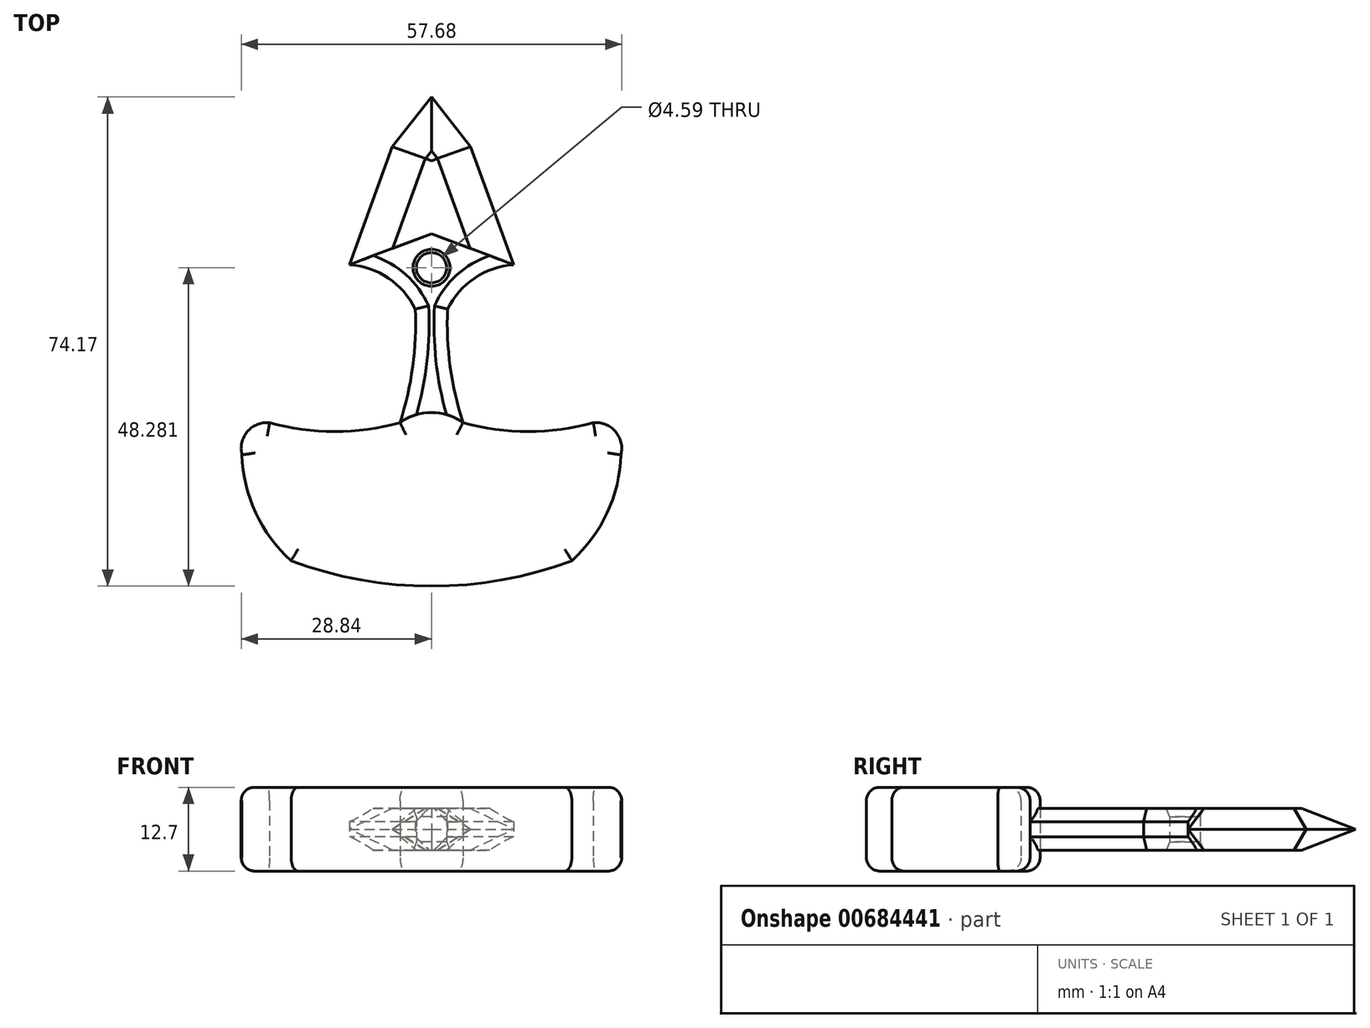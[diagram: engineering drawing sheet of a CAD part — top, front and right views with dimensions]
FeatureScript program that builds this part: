
annotation { "Feature Type Name" : "Feature", "Feature Type Description" : "" }
export const myFeature = defineFeature(function(context is Context, id is Id, definition is map)
    precondition{}
    {
        {
            var Q0;
            Q0=qCreatedBy(makeId("Top.planeOp"),FACE);
            var sketch = newSketch(context, id + "F0", { "sketchPlane" : qUnion([Q0])});
            skPoint(sketch, "E0.middle", {"position": v(0, 0) * mm});
            skLineSegment(sketch, "E1", {"start": v(0, 38.1) * mm, "end": v(5.93, 30.59) * mm});
            skLineSegment(sketch, "E2", {"start": v(5.93, 30.59) * mm, "end": v(12.44, 12.68) * mm});
            skLineSegment(sketch, "E3.MirrorCS", {"start": v(0, 38.1) * mm, "end": v(-5.93, 30.59) * mm});
            skLineSegment(sketch, "E4.MirrorCS", {"start": v(-5.93, 30.59) * mm, "end": v(-12.44, 12.68) * mm});
            skArc(sketch, "E5", {"start": v(-2.44, 5.93) * mm, "mid": v(-6.54, 10.65) * mm, "end": v(-12.44, 12.68) * mm});
            skArc(sketch, "E6.MirrorCS", {"start": v(2.44, 5.93) * mm, "mid": v(6.54, 10.65) * mm, "end": v(12.44, 12.68) * mm});
            skArc(sketch, "E7", {"start": v(2.44, 5.93) * mm, "mid": v(2.84, -2.78) * mm, "end": v(4.77, -11.28) * mm});
            skArc(sketch, "E8.MirrorCS", {"start": v(-2.44, 5.93) * mm, "mid": v(-2.84, -2.78) * mm, "end": v(-4.77, -11.28) * mm});
            skArc(sketch, "E9", {"start": v(4.77, -11.28) * mm, "mid": v(14.65, -12.62) * mm, "end": v(24.54, -11.28) * mm});
            skArc(sketch, "E10", {"start": v(28.72, -16.16) * mm, "mid": v(27.9, -12.64) * mm, "end": v(24.54, -11.28) * mm});
            skArc(sketch, "E11", {"start": v(21.28, -32.21) * mm, "mid": v(26.64, -24.95) * mm, "end": v(28.72, -16.16) * mm});
            skArc(sketch, "E12.MirrorCS", {"start": v(-4.77, -11.28) * mm, "mid": v(-14.65, -12.62) * mm, "end": v(-24.54, -11.28) * mm});
            skArc(sketch, "E13.MirrorCS", {"start": v(-28.72, -16.16) * mm, "mid": v(-27.9, -12.64) * mm, "end": v(-24.54, -11.28) * mm});
            skArc(sketch, "E14.MirrorCS", {"start": v(-21.28, -32.21) * mm, "mid": v(-26.64, -24.95) * mm, "end": v(-28.72, -16.16) * mm});
            skArc(sketch, "E15", {"start": v(-21.28, -32.21) * mm, "mid": v(0, -36.07) * mm, "end": v(21.28, -32.21) * mm});
            skArc(sketch, "E16", {"start": v(4.77, -11.28) * mm, "mid": v(0, -9.74) * mm, "end": v(-4.77, -11.28) * mm});
            skLineSegment(sketch, "E17", {"start": v(-5.93, 30.59) * mm, "end": v(0, 28.43) * mm});
            skLineSegment(sketch, "E18", {"start": v(0, 28.43) * mm, "end": v(5.93, 30.59) * mm});
            skLineSegment(sketch, "E19", {"start": v(-12.44, 12.68) * mm, "end": v(0, 17.33) * mm});
            skLineSegment(sketch, "E20", {"start": v(0, 17.33) * mm, "end": v(12.44, 12.68) * mm});
            skLineSegment(sketch, "E21", {"start": v(0, 38.1) * mm, "end": v(0, 28.43) * mm});
            skLineSegment(sketch, "E22", {"start": v(0, 17.33) * mm, "end": v(0, 28.43) * mm});
            skCircle(sketch, "E23", {"center": v(0, 12.21) * mm, "radius": 2.3 * mm});
            skSolve(sketch);
        }
        {
            var Q0;
            Q0=makeQuery(id+"F0.imprint","IMPRINT",FACE,{"disambiguationData":[TD([[makeQuery(id+"F0.imprint","IMPRINT",EDGE,{"derivedFrom":sQuery(id+"F0.wireOp",EDGE,"E9")}),-1.0]])]});
            extrude(context, id + "F1", {"entities" : qUnion([Q0]), "depth" : 12.7 * mm, "offsetDistance" : 25.4 * mm});
        }
        {
            var Q0;
            Q0=makeQuery(id+"F0.imprint","IMPRINT",FACE,{"disambiguationData":[TD([[makeQuery(id+"F0.imprint","IMPRINT",EDGE,{"derivedFrom":sQuery(id+"F0.wireOp",EDGE,"E5")}),-1.0]])]});
            extrude(context, id + "F2", {"entities" : qUnion([Q0]), "depth" : 6.35 * mm, "offsetDistance" : 25.4 * mm});
        }
        {
            var Q0;
            Q0=makeQuery(id+"F2.opExtrude","SWEPT_BODY",BODY,{"disambiguationData":[OSD([sQuery(id+"F0.wireOp",EDGE,"E5"),sQuery(id+"F0.wireOp",EDGE,"E6.MirrorCS"),sQuery(id+"F0.wireOp",EDGE,"E7"),sQuery(id+"F0.wireOp",EDGE,"E8.MirrorCS"),sQuery(id+"F0.wireOp",EDGE,"E16"),sQuery(id+"F0.wireOp",EDGE,"E19"),sQuery(id+"F0.wireOp",EDGE,"E20"),sQuery(id+"F0.wireOp",EDGE,"E23")])]});
            transform(context, id + "F3", {"entities" : qUnion([Q0]), "transformType" : TransformType.TRANSLATION_3D, "dx" : 0 * mm, "dy" : 0 * mm, "dz" : 3.17 * mm, "makeCopy" : false});
        }
        {
            var Q0;
            Q0=makeQuery(id+"F0.imprint","IMPRINT",FACE,{"disambiguationData":[TD([[makeQuery(id+"F0.imprint","IMPRINT",EDGE,{"derivedFrom":sQuery(id+"F0.wireOp",EDGE,"E2")}),-1.0]])]});
            var Q1;
            Q1=makeQuery(id+"F0.imprint","IMPRINT",FACE,{"disambiguationData":[TD([[makeQuery(id+"F0.imprint","IMPRINT",EDGE,{"derivedFrom":sQuery(id+"F0.wireOp",EDGE,"E4.MirrorCS")}),1.0]])]});
            extrude(context, id + "F4", {"entities" : qUnion([Q0, Q1]), "depth" : 6.35 * mm, "offsetDistance" : 25.4 * mm});
        }
        {
            var Q0;
            Q0=makeQuery(id+"F4.opExtrude","SWEPT_BODY",BODY,{"disambiguationData":[OSD([sQuery(id+"F0.wireOp",EDGE,"E2"),sQuery(id+"F0.wireOp",EDGE,"E4.MirrorCS"),sQuery(id+"F0.wireOp",EDGE,"E17"),sQuery(id+"F0.wireOp",EDGE,"E18"),sQuery(id+"F0.wireOp",EDGE,"E19"),sQuery(id+"F0.wireOp",EDGE,"E20")])]});
            transform(context, id + "F5", {"entities" : qUnion([Q0]), "transformType" : TransformType.TRANSLATION_3D, "dx" : 0 * mm, "dy" : 0 * mm, "dz" : 3.17 * mm, "makeCopy" : false});
        }
        {
            var Q0;
            Q0=makeQuery(id+"F0.imprint","IMPRINT",FACE,{"disambiguationData":[TD([[makeQuery(id+"F0.imprint","IMPRINT",EDGE,{"derivedFrom":sQuery(id+"F0.wireOp",EDGE,"E1")}),-1.0]])]});
            var Q1;
            Q1=makeQuery(id+"F0.imprint","IMPRINT",FACE,{"disambiguationData":[TD([[makeQuery(id+"F0.imprint","IMPRINT",EDGE,{"derivedFrom":sQuery(id+"F0.wireOp",EDGE,"E3.MirrorCS")}),1.0]])]});
            extrude(context, id + "F6", {"entities" : qUnion([Q0, Q1]), "depth" : 6.35 * mm, "offsetDistance" : 25.4 * mm});
        }
        {
            var Q0;
            Q0=makeQuery(id+"F6.opExtrude","SWEPT_BODY",BODY,{"disambiguationData":[OSD([sQuery(id+"F0.wireOp",EDGE,"E1"),sQuery(id+"F0.wireOp",EDGE,"E3.MirrorCS"),sQuery(id+"F0.wireOp",EDGE,"E17"),sQuery(id+"F0.wireOp",EDGE,"E18")])]});
            transform(context, id + "F7", {"entities" : qUnion([Q0]), "transformType" : TransformType.TRANSLATION_3D, "dx" : 0 * mm, "dy" : 0 * mm, "dz" : 3.17 * mm, "makeCopy" : false});
        }
        {
            var Q0;
            Q0=makeQuery(id+"F6.opExtrude","CAP_EDGE",EDGE,{"disambiguationData":[OSD([sQuery(id+"F0.wireOp",EDGE,"E1")])],"isStart":false});
            var Q1;
            Q1=makeQuery(id+"F6.opExtrude","CAP_EDGE",EDGE,{"disambiguationData":[OSD([sQuery(id+"F0.wireOp",EDGE,"E3.MirrorCS")])],"isStart":false});
            var Q2;
            Q2=makeQuery(id+"F6.opExtrude","CAP_EDGE",EDGE,{"disambiguationData":[OSD([sQuery(id+"F0.wireOp",EDGE,"E1")])],"isStart":true});
            var Q3;
            Q3=makeQuery(id+"F6.opExtrude","CAP_EDGE",EDGE,{"disambiguationData":[OSD([sQuery(id+"F0.wireOp",EDGE,"E3.MirrorCS")])],"isStart":true});
            chamfer(context, id + "F8", {"entities" : qUnion([Q0, Q1, Q2, Q3]), "chamferType" : ChamferType.TWO_OFFSETS, "width1" : 3.17 * mm, "oppositeDirection" : false, "width2" : 5.08 * mm, "tangentPropagation" : true});
        }
        {
            var Q0;
            Q0=makeQuery(id+"F4.opExtrude","CAP_EDGE",EDGE,{"disambiguationData":[OSD([sQuery(id+"F0.wireOp",EDGE,"E2")])],"isStart":false});
            var Q1;
            Q1=makeQuery(id+"F4.opExtrude","CAP_EDGE",EDGE,{"disambiguationData":[OSD([sQuery(id+"F0.wireOp",EDGE,"E4.MirrorCS")])],"isStart":false});
            var Q2;
            Q2=makeQuery(id+"F4.opExtrude","CAP_EDGE",EDGE,{"disambiguationData":[OSD([sQuery(id+"F0.wireOp",EDGE,"E2")])],"isStart":true});
            var Q3;
            Q3=makeQuery(id+"F4.opExtrude","CAP_EDGE",EDGE,{"disambiguationData":[OSD([sQuery(id+"F0.wireOp",EDGE,"E4.MirrorCS")])],"isStart":true});
            chamfer(context, id + "F9", {"entities" : qUnion([Q0, Q1, Q2, Q3]), "chamferType" : ChamferType.TWO_OFFSETS, "width1" : 3.17 * mm, "oppositeDirection" : false, "width2" : 5.33 * mm, "tangentPropagation" : true});
        }
        {
            var Q0;
            Q0=makeQuery(id+"F2.opExtrude","CAP_EDGE",EDGE,{"disambiguationData":[OSD([sQuery(id+"F0.wireOp",EDGE,"E6.MirrorCS")])],"isStart":false});
            var Q1;
            Q1=makeQuery(id+"F2.opExtrude","CAP_EDGE",EDGE,{"disambiguationData":[OSD([sQuery(id+"F0.wireOp",EDGE,"E6.MirrorCS")])],"isStart":true});
            var Q2;
            Q2=makeQuery(id+"F2.opExtrude","CAP_EDGE",EDGE,{"disambiguationData":[OSD([sQuery(id+"F0.wireOp",EDGE,"E5")])],"isStart":false});
            var Q3;
            Q3=makeQuery(id+"F2.opExtrude","CAP_EDGE",EDGE,{"disambiguationData":[OSD([sQuery(id+"F0.wireOp",EDGE,"E5")])],"isStart":true});
            var Q4;
            Q4=makeQuery(id+"F2.opExtrude","CAP_EDGE",EDGE,{"disambiguationData":[OSD([sQuery(id+"F0.wireOp",EDGE,"E8.MirrorCS")])],"isStart":false});
            var Q5;
            Q5=makeQuery(id+"F2.opExtrude","CAP_EDGE",EDGE,{"disambiguationData":[OSD([sQuery(id+"F0.wireOp",EDGE,"E7")])],"isStart":false});
            var Q6;
            Q6=makeQuery(id+"F2.opExtrude","CAP_EDGE",EDGE,{"disambiguationData":[OSD([sQuery(id+"F0.wireOp",EDGE,"E8.MirrorCS")])],"isStart":true});
            var Q7;
            Q7=makeQuery(id+"F2.opExtrude","CAP_EDGE",EDGE,{"disambiguationData":[OSD([sQuery(id+"F0.wireOp",EDGE,"E7")])],"isStart":true});
            chamfer(context, id + "F10", {"entities" : qUnion([Q0, Q1, Q2, Q3, Q4, Q5, Q6, Q7]), "width" : 2.03 * mm, "tangentPropagation" : true});
        }
        {
            var Q0;
            Q0=makeQuery(id+"F2.opExtrude","CAP_EDGE",EDGE,{"disambiguationData":[OSD([sQuery(id+"F0.wireOp",EDGE,"E23")])],"isStart":false});
            var Q1;
            Q1=makeQuery(id+"F2.opExtrude","CAP_EDGE",EDGE,{"disambiguationData":[OSD([sQuery(id+"F0.wireOp",EDGE,"E23")])],"isStart":true});
            chamfer(context, id + "F11", {"entities" : qUnion([Q0, Q1]), "chamferType" : ChamferType.TWO_OFFSETS, "width1" : 1.27 * mm, "oppositeDirection" : false, "width2" : 0.5 * mm, "tangentPropagation" : true});
        }
        {
            var Q0;
            Q0=makeQuery(id+"F1.opExtrude","CAP_EDGE",EDGE,{"disambiguationData":[OSD([sQuery(id+"F0.wireOp",EDGE,"E16")])],"isStart":false});
            var Q1;
            Q1=makeQuery(id+"F1.opExtrude","CAP_EDGE",EDGE,{"disambiguationData":[OSD([sQuery(id+"F0.wireOp",EDGE,"E9")])],"isStart":false});
            var Q2;
            Q2=makeQuery(id+"F1.opExtrude","CAP_EDGE",EDGE,{"disambiguationData":[OSD([sQuery(id+"F0.wireOp",EDGE,"E12.MirrorCS")])],"isStart":false});
            var Q3;
            Q3=makeQuery(id+"F1.opExtrude","CAP_EDGE",EDGE,{"disambiguationData":[OSD([sQuery(id+"F0.wireOp",EDGE,"E12.MirrorCS")])],"isStart":true});
            var Q4;
            Q4=makeQuery(id+"F1.opExtrude","CAP_EDGE",EDGE,{"disambiguationData":[OSD([sQuery(id+"F0.wireOp",EDGE,"E9")])],"isStart":true});
            var Q5;
            Q5=makeQuery(id+"F1.opExtrude","CAP_EDGE",EDGE,{"disambiguationData":[OSD([sQuery(id+"F0.wireOp",EDGE,"E10")])],"isStart":false});
            var Q6;
            Q6=makeQuery(id+"F1.opExtrude","CAP_EDGE",EDGE,{"disambiguationData":[OSD([sQuery(id+"F0.wireOp",EDGE,"E10")])],"isStart":true});
            var Q7;
            Q7=makeQuery(id+"F1.opExtrude","CAP_EDGE",EDGE,{"disambiguationData":[OSD([sQuery(id+"F0.wireOp",EDGE,"E16")])],"isStart":true});
            var Q8;
            Q8=makeQuery(id+"F1.opExtrude","CAP_EDGE",EDGE,{"disambiguationData":[OSD([sQuery(id+"F0.wireOp",EDGE,"E13.MirrorCS")])],"isStart":false});
            var Q9;
            Q9=makeQuery(id+"F1.opExtrude","CAP_EDGE",EDGE,{"disambiguationData":[OSD([sQuery(id+"F0.wireOp",EDGE,"E13.MirrorCS")])],"isStart":true});
            var Q10;
            Q10=makeQuery(id+"F1.opExtrude","CAP_EDGE",EDGE,{"disambiguationData":[OSD([sQuery(id+"F0.wireOp",EDGE,"E14.MirrorCS")])],"isStart":false});
            var Q11;
            Q11=makeQuery(id+"F1.opExtrude","CAP_EDGE",EDGE,{"disambiguationData":[OSD([sQuery(id+"F0.wireOp",EDGE,"E14.MirrorCS")])],"isStart":true});
            var Q12;
            Q12=makeQuery(id+"F1.opExtrude","CAP_EDGE",EDGE,{"disambiguationData":[OSD([sQuery(id+"F0.wireOp",EDGE,"E15")])],"isStart":false});
            var Q13;
            Q13=makeQuery(id+"F1.opExtrude","CAP_EDGE",EDGE,{"disambiguationData":[OSD([sQuery(id+"F0.wireOp",EDGE,"E15")])],"isStart":true});
            var Q14;
            Q14=makeQuery(id+"F1.opExtrude","CAP_EDGE",EDGE,{"disambiguationData":[OSD([sQuery(id+"F0.wireOp",EDGE,"E11")])],"isStart":true});
            var Q15;
            Q15=makeQuery(id+"F1.opExtrude","CAP_EDGE",EDGE,{"disambiguationData":[OSD([sQuery(id+"F0.wireOp",EDGE,"E11")])],"isStart":false});
            fillet(context, id + "F12", {"entities" : qUnion([Q0, Q1, Q2, Q3, Q4, Q5, Q6, Q7, Q8, Q9, Q10, Q11, Q12, Q13, Q14, Q15]), "radius" : 2.03 * mm, "tangentPropagation" : true, "allowEdgeOverflow" : false});
        }
    });
